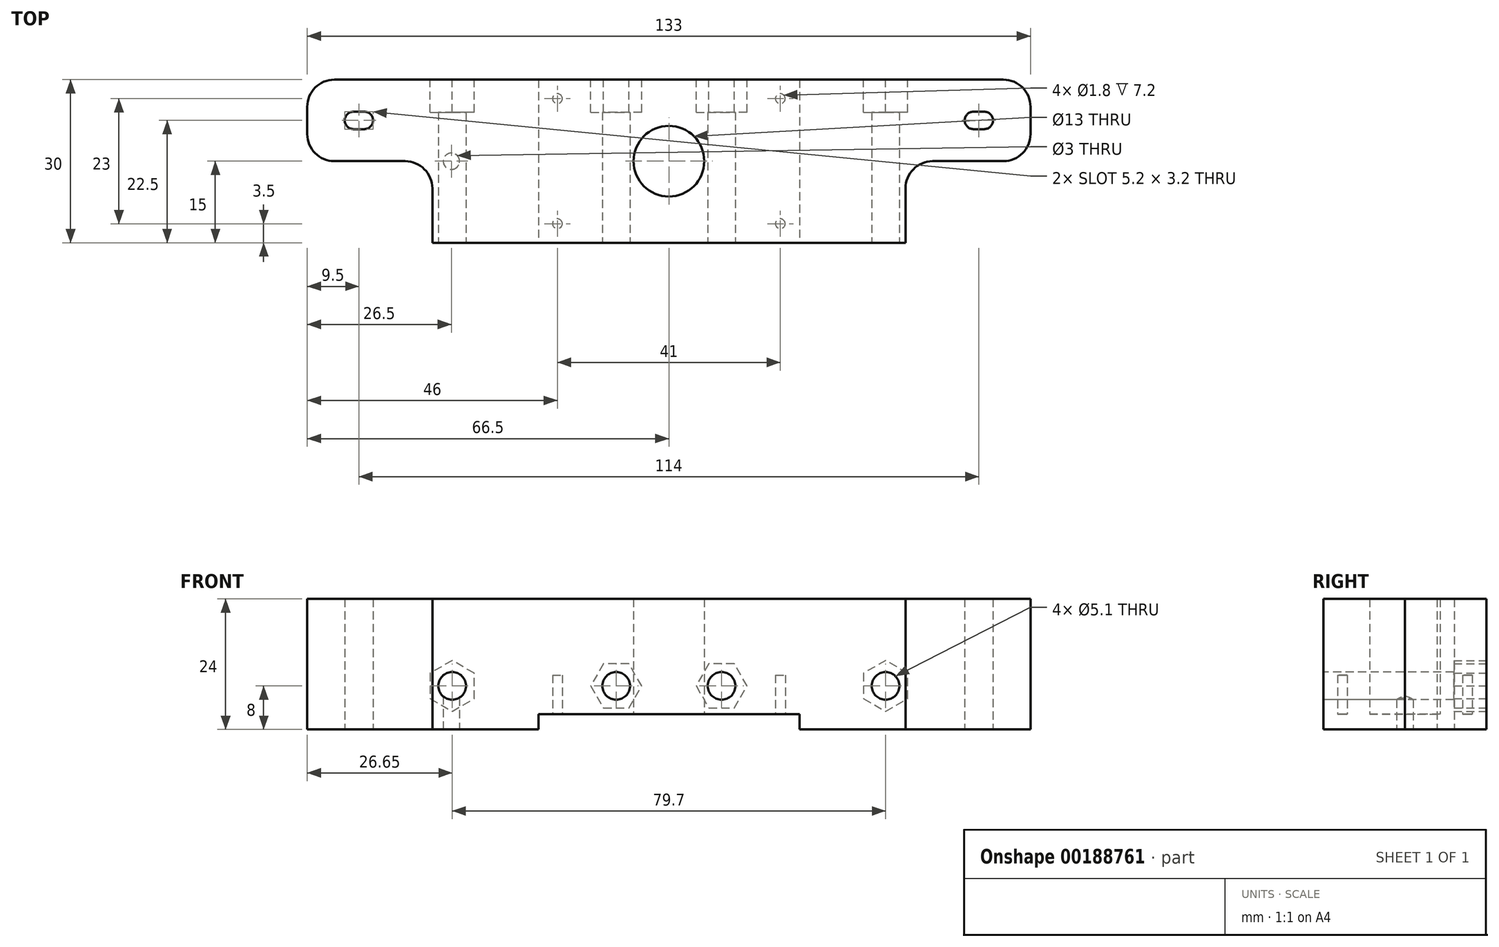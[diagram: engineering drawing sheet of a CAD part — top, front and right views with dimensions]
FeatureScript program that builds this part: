
annotation { "Feature Type Name" : "Feature", "Feature Type Description" : "" }
export const myFeature = defineFeature(function(context is Context, id is Id, definition is map)
    precondition{}
    {
        {
            var Q0;
            Q0=qCreatedBy(makeId("Top.planeOp"),FACE);
            var sketch = newSketch(context, id + "F0", { "sketchPlane" : qUnion([Q0])});
            skLineSegment(sketch, "E0.bottom", {"start": v(43.5, -15) * mm, "end": v(-43.5, -15) * mm});
            skLineSegment(sketch, "E0.top", {"start": v(43.5, 15) * mm, "end": v(-43.5, 15) * mm});
            skLineSegment(sketch, "E0.left", {"start": v(43.5, -15) * mm, "end": v(43.5, 15) * mm});
            skLineSegment(sketch, "E0.right", {"start": v(-43.5, -15) * mm, "end": v(-43.5, 15) * mm});
            skPoint(sketch, "E0.middle", {"position": v(0, 0) * mm});
            skCircle(sketch, "E1", {"center": v(0, 0) * mm, "radius": 6.5 * mm});
            skPoint(sketch, "E2.oppositeSnap0", {"position": v(-43.5, 0) * mm});
            skLineSegment(sketch, "E2.bottom", {"start": v(-43.5, 15) * mm, "end": v(-66.5, 15) * mm});
            skLineSegment(sketch, "E2.top", {"start": v(-43.5, 0) * mm, "end": v(-66.5, 0) * mm});
            skLineSegment(sketch, "E2.left", {"start": v(-43.5, 15) * mm, "end": v(-43.5, 0) * mm});
            skLineSegment(sketch, "E2.right", {"start": v(-66.5, 15) * mm, "end": v(-66.5, 0) * mm});
            skLineSegment(sketch, "E3.bottom", {"start": v(43.5, 15) * mm, "end": v(66.5, 15) * mm});
            skLineSegment(sketch, "E3.top", {"start": v(43.5, 0) * mm, "end": v(66.5, 0) * mm});
            skLineSegment(sketch, "E3.left", {"start": v(43.5, 15) * mm, "end": v(43.5, 0) * mm});
            skLineSegment(sketch, "E3.right", {"start": v(66.5, 15) * mm, "end": v(66.5, 0) * mm});
            skCircle(sketch, "E4", {"center": v(-57, 7.5) * mm, "radius": 1.6 * mm, "construction": true});
            skCircle(sketch, "E5", {"center": v(57, 7.5) * mm, "radius": 1.6 * mm, "construction": true});
            skLineSegment(sketch, "E6", {"start": v(-43.5, 15) * mm, "end": v(43.5, -15) * mm, "construction": true});
            skLineSegment(sketch, "E7", {"start": v(58, 7.5) * mm, "end": v(56, 7.5) * mm, "construction": true});
            skArc(sketch, "E8.0.startCap", {"start": v(58, 9.1) * mm, "mid": v(59.6, 7.5) * mm, "end": v(58, 5.9) * mm});
            skArc(sketch, "E8.0.endCap", {"start": v(56, 5.9) * mm, "mid": v(54.4, 7.5) * mm, "end": v(56, 9.1) * mm});
            skLineSegment(sketch, "E8.0.left", {"start": v(58, 5.9) * mm, "end": v(56, 5.9) * mm});
            skLineSegment(sketch, "E8.0.right", {"start": v(58, 9.1) * mm, "end": v(56, 9.1) * mm});
            skLineSegment(sketch, "E9", {"start": v(-56, 7.5) * mm, "end": v(-58, 7.5) * mm, "construction": true});
            skArc(sketch, "E10.0.startCap", {"start": v(-56, 9.1) * mm, "mid": v(-54.4, 7.5) * mm, "end": v(-56, 5.9) * mm});
            skArc(sketch, "E10.0.endCap", {"start": v(-58, 5.9) * mm, "mid": v(-59.6, 7.5) * mm, "end": v(-58, 9.1) * mm});
            skLineSegment(sketch, "E10.0.left", {"start": v(-56, 5.9) * mm, "end": v(-58, 5.9) * mm});
            skLineSegment(sketch, "E10.0.right", {"start": v(-56, 9.1) * mm, "end": v(-58, 9.1) * mm});
            skPoint(sketch, "E11", {"position": v(-66.5, 7.5) * mm});
            skLineSegment(sketch, "E12", {"start": v(0, -15) * mm, "end": v(0, 15) * mm, "construction": true});
            skSolve(sketch);
        }
        {
            var Q0;
            Q0=makeQuery(id+"F0.imprint","IMPRINT",FACE,{"disambiguationData":[TD([[makeQuery(id+"F0.imprint","IMPRINT",EDGE,{"derivedFrom":sQuery(id+"F0.wireOp",EDGE,"E2.bottom")}),1.0]])]});
            var Q1;
            Q1=makeQuery(id+"F0.imprint","IMPRINT",FACE,{"disambiguationData":[TD([[makeQuery(id+"F0.imprint","IMPRINT",EDGE,{"derivedFrom":sQuery(id+"F0.wireOp",EDGE,"E0.bottom")}),-1.0]])]});
            var Q2;
            Q2=makeQuery(id+"F0.imprint","IMPRINT",FACE,{"disambiguationData":[TD([[makeQuery(id+"F0.imprint","IMPRINT",EDGE,{"derivedFrom":sQuery(id+"F0.wireOp",EDGE,"E3.bottom")}),-1.0]])]});
            extrude(context, id + "F1", {"entities" : qUnion([Q0, Q1, Q2]), "flatOperationType" : FlatOperationType.REMOVE, "depth" : 24 * mm, "offsetDistance" : 25 * mm, "domain" : OperationDomain.MODEL});
        }
        {
            var Q0;
            Q0=makeQuery(id+"F1.opExtrude","SWEPT_FACE",FACE,{"disambiguationData":[OSD([sQuery(id+"F0.wireOp",EDGE,"E0.bottom")])]});
            var sketch = newSketch(context, id + "F2", { "sketchPlane" : qUnion([Q0])});
            skLineSegment(sketch, "E13", {"start": v(-39.85, 8) * mm, "end": v(39.85, 8) * mm, "construction": true});
            skCircle(sketch, "E14", {"center": v(-39.85, 8) * mm, "radius": 2.55 * mm});
            skCircle(sketch, "E15", {"center": v(39.85, 8) * mm, "radius": 2.55 * mm});
            skLineSegment(sketch, "E16", {"start": v(0, 24) * mm, "end": v(0, 0) * mm, "construction": true});
            skCircle(sketch, "E17", {"center": v(-9.7, 8) * mm, "radius": 2.55 * mm});
            skCircle(sketch, "E18", {"center": v(9.69, 8) * mm, "radius": 2.55 * mm});
            skSolve(sketch);
        }
        {
            var Q0;
            Q0=makeQuery(id+"F2.imprint","IMPRINT",FACE,{"disambiguationData":[TD([[makeQuery(id+"F2.imprint","IMPRINT",EDGE,{"derivedFrom":sQuery(id+"F2.wireOp",EDGE,"E14")}),1.0]])]});
            var Q1;
            Q1=makeQuery(id+"F2.imprint","IMPRINT",FACE,{"disambiguationData":[TD([[makeQuery(id+"F2.imprint","IMPRINT",EDGE,{"derivedFrom":sQuery(id+"F2.wireOp",EDGE,"E15")}),1.0]])]});
            var Q2;
            Q2=makeQuery(id+"F2.imprint","IMPRINT",FACE,{"disambiguationData":[TD([[makeQuery(id+"F2.imprint","IMPRINT",EDGE,{"derivedFrom":sQuery(id+"F2.wireOp",EDGE,"E17")}),1.0]])]});
            var Q3;
            Q3=makeQuery(id+"F2.imprint","IMPRINT",FACE,{"disambiguationData":[TD([[makeQuery(id+"F2.imprint","IMPRINT",EDGE,{"derivedFrom":sQuery(id+"F2.wireOp",EDGE,"E18")}),1.0]])]});
            extrude(context, id + "F3", {"entities" : qUnion([Q0, Q1, Q2, Q3]), "operationType" : NewBodyOperationType.REMOVE, "endBound" : BoundingType.UP_TO_NEXT, "oppositeDirection" : true, "depth" : 8 * mm, "offsetDistance" : 25 * mm});
        }
        {
            var Q0;
            Q0=makeQuery(id+"F1.opExtrude","CAP_FACE",FACE,{"disambiguationData":[OSD([sQuery(id+"F0.wireOp",EDGE,"E0.bottom"),sQuery(id+"F0.wireOp",EDGE,"E0.top"),sQuery(id+"F0.wireOp",EDGE,"E0.left"),sQuery(id+"F0.wireOp",EDGE,"E0.right"),sQuery(id+"F0.wireOp",EDGE,"E1")])],"isStart":true});
            var sketch = newSketch(context, id + "F4", { "sketchPlane" : qUnion([Q0])});
            skLineSegment(sketch, "E19.bottom", {"start": v(20.5, -11.5) * mm, "end": v(-20.5, -11.5) * mm, "construction": true});
            skLineSegment(sketch, "E19.top", {"start": v(20.5, 11.5) * mm, "end": v(-20.5, 11.5) * mm, "construction": true});
            skLineSegment(sketch, "E19.left", {"start": v(20.5, -11.5) * mm, "end": v(20.5, 11.5) * mm, "construction": true});
            skLineSegment(sketch, "E19.right", {"start": v(-20.5, -11.5) * mm, "end": v(-20.5, 11.5) * mm, "construction": true});
            skPoint(sketch, "E19.middle", {"position": v(0, 0) * mm});
            skCircle(sketch, "E20", {"center": v(-20.5, 11.5) * mm, "radius": 0.9 * mm});
            skCircle(sketch, "E21", {"center": v(20.5, 11.5) * mm, "radius": 0.9 * mm});
            skCircle(sketch, "E22", {"center": v(20.5, -11.5) * mm, "radius": 0.9 * mm});
            skCircle(sketch, "E23", {"center": v(-20.5, -11.5) * mm, "radius": 0.9 * mm});
            skSolve(sketch);
        }
        {
            var Q0;
            Q0=makeQuery(id+"F4.imprint","IMPRINT",FACE,{"disambiguationData":[TD([[makeQuery(id+"F4.imprint","IMPRINT",EDGE,{"derivedFrom":sQuery(id+"F4.wireOp",EDGE,"E20")}),1.0]])]});
            var Q1;
            Q1=makeQuery(id+"F4.imprint","IMPRINT",FACE,{"disambiguationData":[TD([[makeQuery(id+"F4.imprint","IMPRINT",EDGE,{"derivedFrom":sQuery(id+"F4.wireOp",EDGE,"E23")}),1.0]])]});
            var Q2;
            Q2=makeQuery(id+"F4.imprint","IMPRINT",FACE,{"disambiguationData":[TD([[makeQuery(id+"F4.imprint","IMPRINT",EDGE,{"derivedFrom":sQuery(id+"F4.wireOp",EDGE,"E22")}),1.0]])]});
            var Q3;
            Q3=makeQuery(id+"F4.imprint","IMPRINT",FACE,{"disambiguationData":[TD([[makeQuery(id+"F4.imprint","IMPRINT",EDGE,{"derivedFrom":sQuery(id+"F4.wireOp",EDGE,"E21")}),1.0]])]});
            extrude(context, id + "F5", {"entities" : qUnion([Q0, Q1, Q2, Q3]), "operationType" : NewBodyOperationType.REMOVE, "oppositeDirection" : true, "depth" : 10 * mm, "offsetDistance" : 25 * mm});
        }
        {
            var Q0;
            Q0=makeQuery(id+"F1.opExtrude","CAP_FACE",FACE,{"disambiguationData":[OSD([sQuery(id+"F0.wireOp",EDGE,"E0.bottom"),sQuery(id+"F0.wireOp",EDGE,"E0.top"),sQuery(id+"F0.wireOp",EDGE,"E0.left"),sQuery(id+"F0.wireOp",EDGE,"E0.right"),sQuery(id+"F0.wireOp",EDGE,"E1")])],"isStart":true});
            var sketch = newSketch(context, id + "F6", { "sketchPlane" : qUnion([Q0])});
            skLineSegment(sketch, "E24", {"start": v(24, -15) * mm, "end": v(24, 15) * mm});
            skLineSegment(sketch, "E25", {"start": v(-24, -15) * mm, "end": v(-24, 15) * mm});
            skLineSegment(sketch, "E26", {"start": v(0, 15) * mm, "end": v(0, -15) * mm, "construction": true});
            skSolve(sketch);
        }
        {
            var Q0;
            {var subQ1=sQuery(id+"F6.wireOp",EDGE,"E24");Q0=makeQuery(id+"F6.imprint","IMPRINT",FACE,{"disambiguationData":[TD([[makeQuery(id+"F6.imprint","IMPRINT",EDGE,{"derivedFrom":subQ1}),1.0]])]});}
            extrude(context, id + "F7", {"entities" : qUnion([Q0]), "operationType" : NewBodyOperationType.REMOVE, "oppositeDirection" : true, "depth" : 2.8 * mm, "offsetDistance" : 25 * mm});
        }
        {
            var Q0;
            Q0=qCreatedBy(makeId("Top.planeOp"),FACE);
            var sketch = newSketch(context, id + "F8", { "sketchPlane" : qUnion([Q0])});
            skLineSegment(sketch, "E27", {"start": v(-43.5, 0) * mm, "end": v(0, 0) * mm, "construction": true});
            skCircle(sketch, "E28", {"center": v(-40, 0) * mm, "radius": 1.5 * mm});
            skSolve(sketch);
        }
        {
            var Q0;
            Q0=makeQuery(id+"F8.imprint","IMPRINT",FACE,{"disambiguationData":[TD([[makeQuery(id+"F8.imprint","IMPRINT",EDGE,{"derivedFrom":sQuery(id+"F8.wireOp",EDGE,"E28")}),1.0]])]});
            var Q1;
            Q1=sQuery(id+"F8.wireOp",EDGE,"E28");
            extrude(context, id + "F9", {"entities" : qUnion([Q0]), "operationType" : NewBodyOperationType.REMOVE, "flatOperationType" : FlatOperationType.REMOVE, "surfaceEntities" : qUnion([Q1]), "depth" : 8 * mm, "offsetDistance" : 25 * mm, "domain" : OperationDomain.MODEL});
        }
        {
            var Q0;
            Q0=makeQuery(id+"F1.opExtrude","SWEPT_FACE",FACE,{"disambiguationData":[OSD([sQuery(id+"F0.wireOp",EDGE,"E0.top"),sQuery(id+"F0.wireOp",EDGE,"E2.bottom"),sQuery(id+"F0.wireOp",EDGE,"E3.bottom")])]});
            var sketch = newSketch(context, id + "F10", { "sketchPlane" : qUnion([Q0])});
            skCircle(sketch, "E29.cCircle", {"center": v(-39.85, 8) * mm, "radius": 4.05 * mm, "construction": true});
            skLineSegment(sketch, "E29.0", {"start": v(-35.8, 5.66) * mm, "end": v(-39.85, 3.32) * mm});
            skLineSegment(sketch, "E29.1", {"start": v(-39.85, 3.32) * mm, "end": v(-43.9, 5.66) * mm});
            skLineSegment(sketch, "E29.2", {"start": v(-43.9, 5.66) * mm, "end": v(-43.9, 10.34) * mm});
            skLineSegment(sketch, "E29.3", {"start": v(-43.9, 10.34) * mm, "end": v(-39.85, 12.68) * mm});
            skLineSegment(sketch, "E29.4", {"start": v(-39.85, 12.68) * mm, "end": v(-35.8, 10.34) * mm});
            skLineSegment(sketch, "E29.5", {"start": v(-35.8, 10.34) * mm, "end": v(-35.8, 5.66) * mm});
            skPoint(sketch, "E29.0.midPoint", {"position": v(-37.83, 4.5) * mm});
            skCircle(sketch, "E30.cCircle", {"center": v(-9.69, 8) * mm, "radius": 4.05 * mm, "construction": true});
            skLineSegment(sketch, "E30.0", {"start": v(-5.01, 8) * mm, "end": v(-7.35, 3.95) * mm});
            skLineSegment(sketch, "E30.1", {"start": v(-7.35, 3.95) * mm, "end": v(-12.03, 3.95) * mm});
            skLineSegment(sketch, "E30.2", {"start": v(-12.03, 3.95) * mm, "end": v(-14.37, 8) * mm});
            skLineSegment(sketch, "E30.3", {"start": v(-14.37, 8) * mm, "end": v(-12.03, 12.05) * mm});
            skLineSegment(sketch, "E30.4", {"start": v(-12.03, 12.05) * mm, "end": v(-7.35, 12.05) * mm});
            skLineSegment(sketch, "E30.5", {"start": v(-7.35, 12.05) * mm, "end": v(-5.01, 8) * mm});
            skPoint(sketch, "E30.0.midPoint", {"position": v(-6.18, 5.98) * mm});
            skCircle(sketch, "E31.cCircle", {"center": v(9.7, 8) * mm, "radius": 4.05 * mm, "construction": true});
            skLineSegment(sketch, "E31.0", {"start": v(14.37, 8) * mm, "end": v(12.03, 3.95) * mm});
            skLineSegment(sketch, "E31.1", {"start": v(12.03, 3.95) * mm, "end": v(7.35, 3.95) * mm});
            skLineSegment(sketch, "E31.2", {"start": v(7.35, 3.95) * mm, "end": v(5.01, 8) * mm});
            skLineSegment(sketch, "E31.3", {"start": v(5.01, 8) * mm, "end": v(7.35, 12.05) * mm});
            skLineSegment(sketch, "E31.4", {"start": v(7.35, 12.05) * mm, "end": v(12.03, 12.05) * mm});
            skLineSegment(sketch, "E31.5", {"start": v(12.03, 12.05) * mm, "end": v(14.37, 8) * mm});
            skPoint(sketch, "E31.0.midPoint", {"position": v(13.2, 5.98) * mm});
            skCircle(sketch, "E32.cCircle", {"center": v(39.85, 8) * mm, "radius": 4.05 * mm, "construction": true});
            skLineSegment(sketch, "E32.0", {"start": v(43.9, 5.66) * mm, "end": v(39.85, 3.32) * mm});
            skLineSegment(sketch, "E32.1", {"start": v(39.85, 3.32) * mm, "end": v(35.8, 5.66) * mm});
            skLineSegment(sketch, "E32.2", {"start": v(35.8, 5.66) * mm, "end": v(35.8, 10.34) * mm});
            skLineSegment(sketch, "E32.3", {"start": v(35.8, 10.34) * mm, "end": v(39.85, 12.68) * mm});
            skLineSegment(sketch, "E32.4", {"start": v(39.85, 12.68) * mm, "end": v(43.9, 10.34) * mm});
            skLineSegment(sketch, "E32.5", {"start": v(43.9, 10.34) * mm, "end": v(43.9, 5.66) * mm});
            skPoint(sketch, "E32.0.midPoint", {"position": v(41.87, 4.5) * mm});
            skSolve(sketch);
        }
        {
            var Q0;
            Q0=makeQuery(id+"F10.imprint","IMPRINT",FACE,{"disambiguationData":[TD([[makeQuery(id+"F10.imprint","IMPRINT",EDGE,{"derivedFrom":sQuery(id+"F10.wireOp",EDGE,"E29.0")}),-1.0]])]});
            var Q1;
            Q1=makeQuery(id+"F10.imprint","IMPRINT",FACE,{"disambiguationData":[TD([[makeQuery(id+"F10.imprint","IMPRINT",EDGE,{"derivedFrom":sQuery(id+"F10.wireOp",EDGE,"E30.0")}),-1.0]])]});
            var Q2;
            Q2=makeQuery(id+"F10.imprint","IMPRINT",FACE,{"disambiguationData":[TD([[makeQuery(id+"F10.imprint","IMPRINT",EDGE,{"derivedFrom":sQuery(id+"F10.wireOp",EDGE,"E31.0")}),-1.0]])]});
            var Q3;
            Q3=makeQuery(id+"F10.imprint","IMPRINT",FACE,{"disambiguationData":[TD([[makeQuery(id+"F10.imprint","IMPRINT",EDGE,{"derivedFrom":sQuery(id+"F10.wireOp",EDGE,"E32.0")}),-1.0]])]});
            extrude(context, id + "F11", {"entities" : qUnion([Q0, Q1, Q2, Q3]), "operationType" : NewBodyOperationType.REMOVE, "oppositeDirection" : true, "depth" : 6 * mm, "offsetDistance" : 25 * mm});
        }
        {
            var Q0;
            Q0=makeQuery(id+"F1.opExtrude","SWEPT_EDGE",EDGE,{"disambiguationData":[OSD([sQuery(id+"F0.wireOp",EDGE,"E2.top"),sQuery(id+"F0.wireOp",EDGE,"E2.right")])]});
            var Q1;
            Q1=makeQuery(id+"F1.opExtrude","SWEPT_EDGE",EDGE,{"disambiguationData":[OSD([sQuery(id+"F0.wireOp",EDGE,"E0.right"),sQuery(id+"F0.wireOp",EDGE,"E2.top"),sQuery(id+"F0.wireOp",EDGE,"E2.left")])]});
            var Q2;
            Q2=makeQuery(id+"F1.opExtrude","SWEPT_EDGE",EDGE,{"disambiguationData":[OSD([sQuery(id+"F0.wireOp",EDGE,"E2.bottom"),sQuery(id+"F0.wireOp",EDGE,"E2.right")])]});
            var Q3;
            Q3=makeQuery(id+"F1.opExtrude","SWEPT_EDGE",EDGE,{"disambiguationData":[OSD([sQuery(id+"F0.wireOp",EDGE,"E0.left"),sQuery(id+"F0.wireOp",EDGE,"E3.top"),sQuery(id+"F0.wireOp",EDGE,"E3.left")])]});
            var Q4;
            Q4=makeQuery(id+"F1.opExtrude","SWEPT_EDGE",EDGE,{"disambiguationData":[OSD([sQuery(id+"F0.wireOp",EDGE,"E3.top"),sQuery(id+"F0.wireOp",EDGE,"E3.right")])]});
            var Q5;
            Q5=makeQuery(id+"F1.opExtrude","SWEPT_EDGE",EDGE,{"disambiguationData":[OSD([sQuery(id+"F0.wireOp",EDGE,"E3.bottom"),sQuery(id+"F0.wireOp",EDGE,"E3.right")])]});
            fillet(context, id + "F12", {"entities" : qUnion([Q0, Q1, Q2, Q3, Q4, Q5]), "radius" : 5 * mm, "tangentPropagation" : true, "allowEdgeOverflow" : false});
        }
    });
